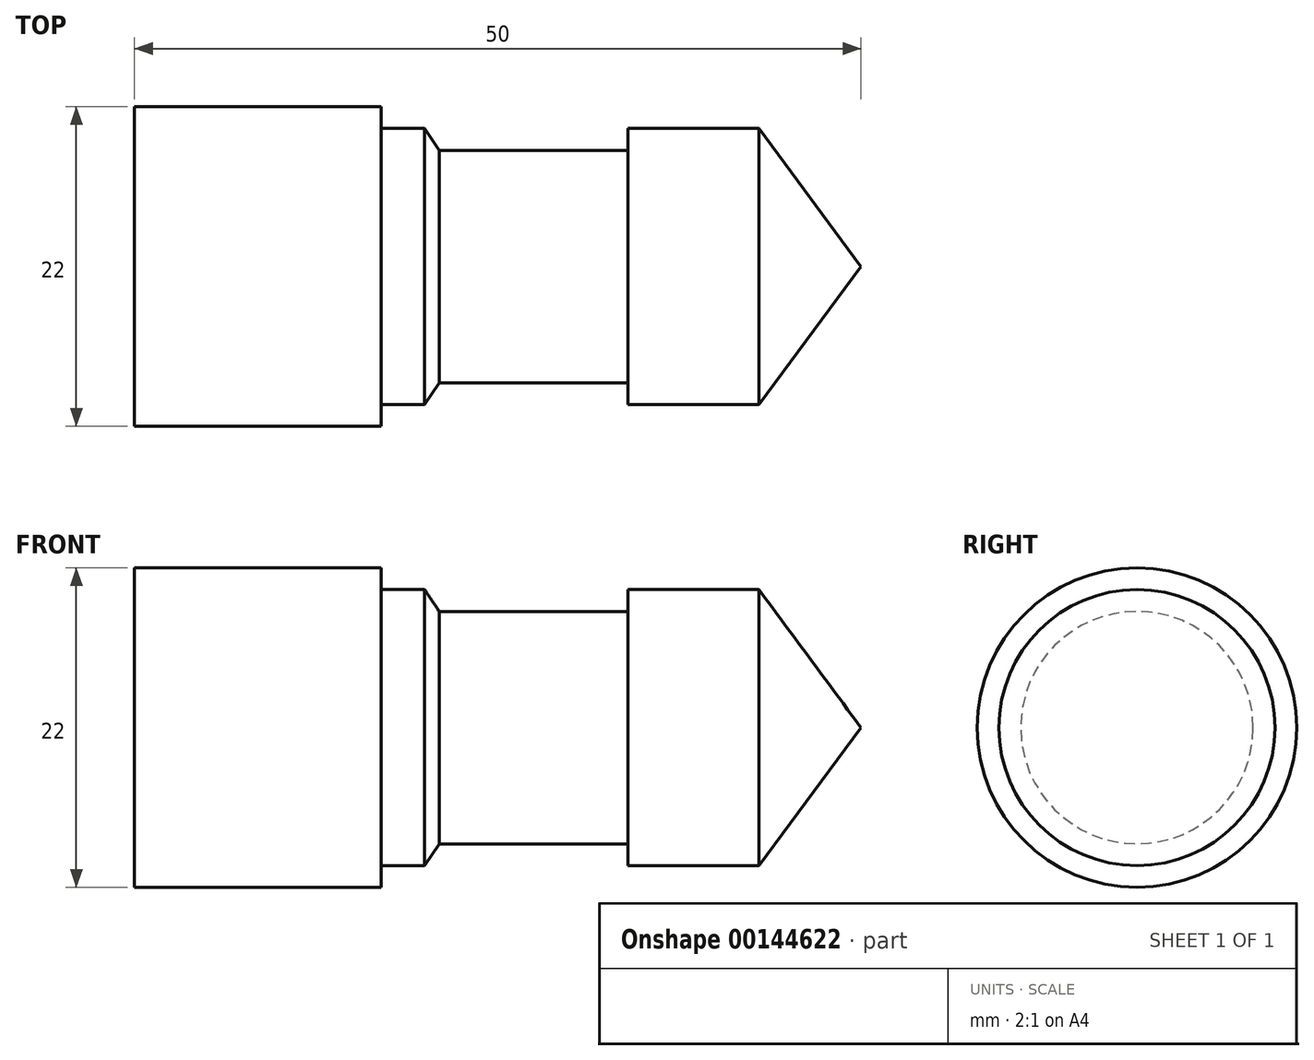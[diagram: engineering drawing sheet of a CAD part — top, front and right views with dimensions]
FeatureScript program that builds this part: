
annotation { "Feature Type Name" : "Feature", "Feature Type Description" : "" }
export const myFeature = defineFeature(function(context is Context, id is Id, definition is map)
    precondition{}
    {
        {
            var Q0;
            Q0=qCreatedBy(makeId("Top.planeOp"),FACE);
            var sketch = newSketch(context, id + "F0", { "sketchPlane" : qUnion([Q0])});
            skLineSegment(sketch, "E0", {"start": v(0, 0) * mm, "end": v(-7.03, 9.5) * mm});
            skLineSegment(sketch, "E1", {"start": v(-7.03, 9.5) * mm, "end": v(-16.03, 9.5) * mm});
            skLineSegment(sketch, "E2", {"start": v(-16.03, 9.5) * mm, "end": v(-16.03, 8) * mm});
            skLineSegment(sketch, "E3", {"start": v(-16.03, 8) * mm, "end": v(-29.03, 8) * mm});
            skLineSegment(sketch, "E4", {"start": v(-29.03, 8) * mm, "end": v(-30.03, 9.5) * mm});
            skLineSegment(sketch, "E5", {"start": v(-30.03, 9.5) * mm, "end": v(-33.03, 9.5) * mm});
            skLineSegment(sketch, "E6", {"start": v(-33.03, 9.5) * mm, "end": v(-33.03, 11) * mm});
            skLineSegment(sketch, "E7", {"start": v(-33.03, 11) * mm, "end": v(-50, 11) * mm});
            skLineSegment(sketch, "E8", {"start": v(-50, 11) * mm, "end": v(-50, 0) * mm});
            skLineSegment(sketch, "E9", {"start": v(-50, 0) * mm, "end": v(0, 0) * mm});
            skSolve(sketch);
        }
        {
            var Q0;
            Q0 = qSketchRegion(id + "F0", true);
            var Q1;
            Q1=sQuery(id+"F0.wireOp",EDGE,"E9");
            revolve(context, id + "F1", {"entities" : qUnion([Q0]), "axis" : qUnion([Q1]), "revolveType" : RevolveType.FULL});
        }
    });
